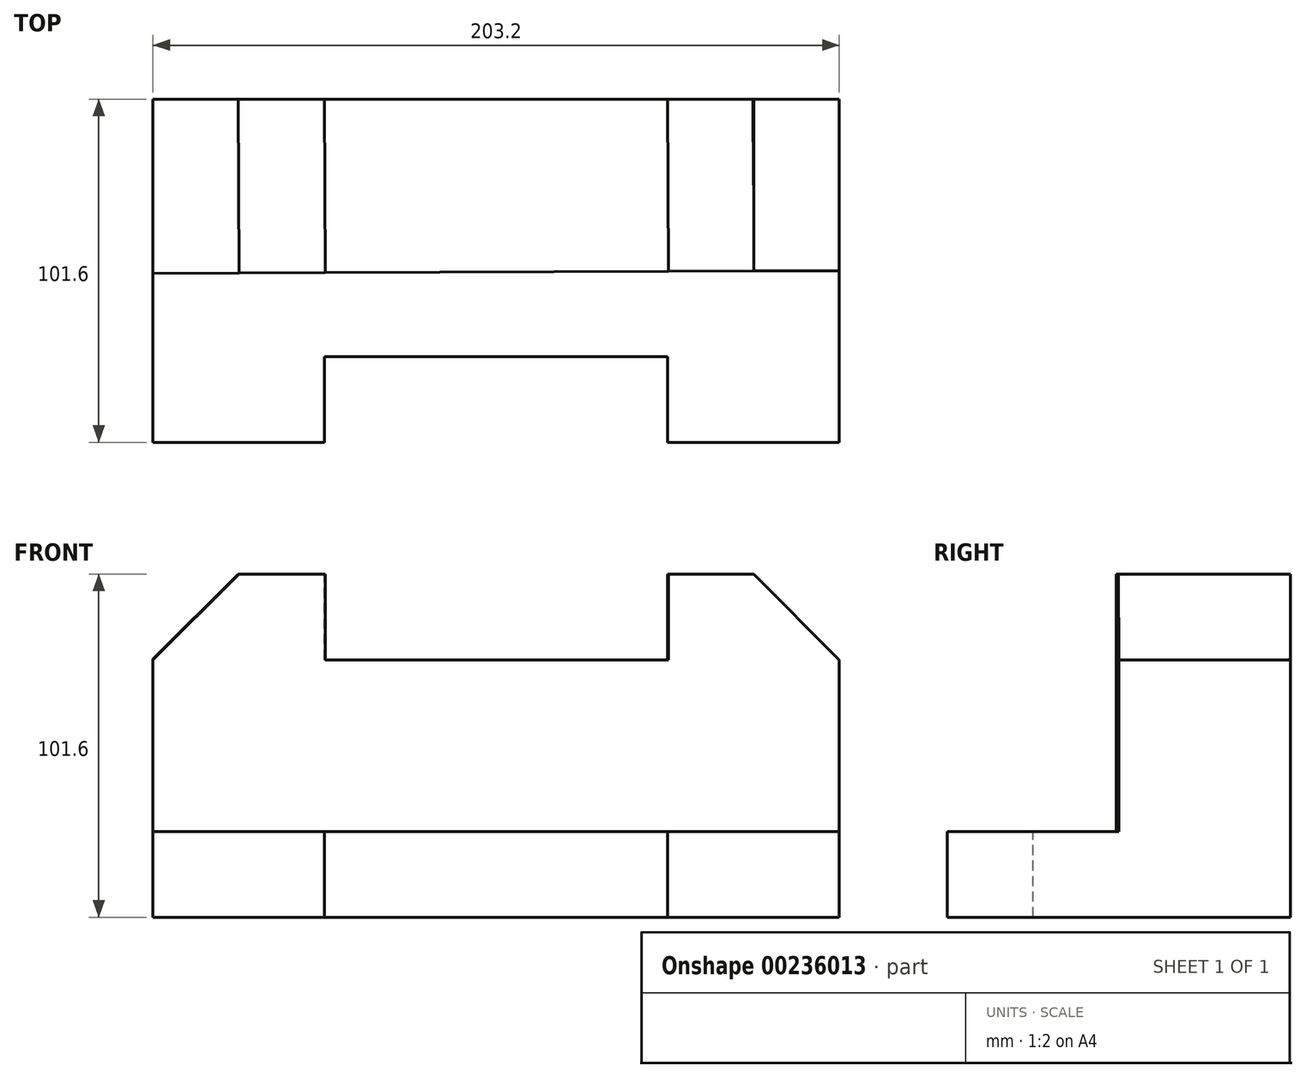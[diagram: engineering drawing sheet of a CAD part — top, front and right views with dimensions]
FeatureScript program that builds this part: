
annotation { "Feature Type Name" : "Feature", "Feature Type Description" : "" }
export const myFeature = defineFeature(function(context is Context, id is Id, definition is map)
    precondition{}
    {
        {
            var Q0;
            Q0=qCreatedBy(makeId("Top.planeOp"),FACE);
            var sketch = newSketch(context, id + "F0", { "sketchPlane" : qUnion([Q0])});
            skLineSegment(sketch, "E0.bottom", {"start": v(-129.83, -49.96) * mm, "end": v(73.37, -49.96) * mm});
            skLineSegment(sketch, "E0.top", {"start": v(-129.83, 51.64) * mm, "end": v(73.37, 51.64) * mm});
            skLineSegment(sketch, "E0.left", {"start": v(-129.83, -49.96) * mm, "end": v(-129.83, 51.64) * mm});
            skLineSegment(sketch, "E0.right", {"start": v(73.37, -49.96) * mm, "end": v(73.37, 51.64) * mm});
            skSolve(sketch);
        }
        {
            var Q0;
            Q0=makeQuery(id+"F0.imprint","IMPRINT",FACE,{"disambiguationData":[TD([[makeQuery(id+"F0.imprint","IMPRINT",EDGE,{"derivedFrom":sQuery(id+"F0.wireOp",EDGE,"E0.bottom")}),1.0]])]});
            extrude(context, id + "F1", {"entities" : qUnion([Q0]), "depth" : 101.6 * mm});
        }
        {
            var Q0;
            Q0=makeQuery(id+"F1.opExtrude","CAP_FACE",FACE,{"disambiguationData":[OSD([sQuery(id+"F0.wireOp",EDGE,"E0.bottom"),sQuery(id+"F0.wireOp",EDGE,"E0.top"),sQuery(id+"F0.wireOp",EDGE,"E0.left"),sQuery(id+"F0.wireOp",EDGE,"E0.right")])],"isStart":false});
            var sketch = newSketch(context, id + "F2", { "sketchPlane" : qUnion([Q0])});
            skLineSegment(sketch, "E1", {"start": v(73.37, -49.96) * mm, "end": v(73.37, 0.84) * mm});
            skLineSegment(sketch, "E2", {"start": v(73.37, 0.84) * mm, "end": v(-129.83, 0) * mm});
            skSolve(sketch);
        }
        {
            var Q0;
            Q0=makeQuery(id+"F2.imprint","IMPRINT",FACE,{"disambiguationData":[TD([[makeQuery(id+"F2.imprint","IMPRINT",EDGE,{"derivedFrom":sQuery(id+"F2.wireOp",EDGE,"E1")}),1.0]])]});
            extrude(context, id + "F3", {"entities" : qUnion([Q0]), "operationType" : NewBodyOperationType.REMOVE, "oppositeDirection" : true, "depth" : 76.2 * mm});
        }
        {
            var Q0;
            Q0=makeQuery(id+"F3.boolean.opBoolean","COPY",FACE,{"derivedFrom":makeQuery(id+"F3.opExtrude","CAP_FACE",FACE,{"disambiguationData":[OSD([sQuery(id+"F0.wireOp",EDGE,"E0.bottom"),sQuery(id+"F0.wireOp",EDGE,"E0.left"),sQuery(id+"F2.wireOp",EDGE,"E1"),sQuery(id+"F2.wireOp",EDGE,"E2")])],"isStart":false})});
            var sketch = newSketch(context, id + "F4", { "sketchPlane" : qUnion([Q0])});
            skLineSegment(sketch, "E3", {"start": v(-129.83, -49.96) * mm, "end": v(-79.03, -49.96) * mm});
            skLineSegment(sketch, "E4", {"start": v(73.37, -49.96) * mm, "end": v(22.57, -49.96) * mm});
            skLineSegment(sketch, "E5", {"start": v(-79.03, -49.96) * mm, "end": v(22.57, -49.96) * mm});
            skLineSegment(sketch, "E6", {"start": v(-79.03, -49.96) * mm, "end": v(-79.03, -24.56) * mm});
            skLineSegment(sketch, "E7", {"start": v(22.57, -49.96) * mm, "end": v(22.57, -24.56) * mm});
            skLineSegment(sketch, "E8", {"start": v(-79.03, -24.56) * mm, "end": v(22.57, -24.56) * mm});
            skSolve(sketch);
        }
        {
            var Q0;
            Q0=makeQuery(id+"F4.imprint","IMPRINT",FACE,{"disambiguationData":[TD([[makeQuery(id+"F4.imprint","IMPRINT",EDGE,{"derivedFrom":sQuery(id+"F4.wireOp",EDGE,"E5")}),1.0]])]});
            extrude(context, id + "F5", {"entities" : qUnion([Q0]), "operationType" : NewBodyOperationType.REMOVE, "oppositeDirection" : true, "depth" : 25.4 * mm});
        }
        {
            var Q0;
            Q0=makeQuery(id+"F1.opExtrude","CAP_FACE",FACE,{"disambiguationData":[OSD([sQuery(id+"F0.wireOp",EDGE,"E0.bottom"),sQuery(id+"F0.wireOp",EDGE,"E0.top"),sQuery(id+"F0.wireOp",EDGE,"E0.left"),sQuery(id+"F0.wireOp",EDGE,"E0.right")])],"isStart":false});
            var sketch = newSketch(context, id + "F6", { "sketchPlane" : qUnion([Q0])});
            skLineSegment(sketch, "E9", {"start": v(73.37, 51.64) * mm, "end": v(22.57, 51.64) * mm});
            skLineSegment(sketch, "E10", {"start": v(-129.83, 51.64) * mm, "end": v(-79.03, 51.64) * mm});
            skLineSegment(sketch, "E11", {"start": v(-79.03, 51.64) * mm, "end": v(-78.82, 0) * mm});
            skLineSegment(sketch, "E12", {"start": v(22.57, 51.64) * mm, "end": v(22.78, 0) * mm});
            skLineSegment(sketch, "E13", {"start": v(-79.03, 51.64) * mm, "end": v(22.57, 51.64) * mm});
            skSolve(sketch);
        }
        {
            var Q0;
            {var subQ0=sQuery(id+"F6.wireOp",EDGE,"E13");Q0=makeQuery(id+"F6.imprint","IMPRINT",FACE,{"disambiguationData":[TD([[makeQuery(id+"F6.imprint","IMPRINT",EDGE,{"derivedFrom":subQ0}),-1.0]])]});}
            extrude(context, id + "F7", {"entities" : qUnion([Q0]), "operationType" : NewBodyOperationType.REMOVE, "oppositeDirection" : true, "depth" : 25.4 * mm});
        }
        {
            var Q0;
            Q0=makeQuery(id+"F3.boolean.opBoolean","COPY",FACE,{"derivedFrom":makeQuery(id+"F3.opExtrude","SWEPT_FACE",FACE,{"disambiguationData":[OSD([sQuery(id+"F2.wireOp",EDGE,"E2")])]})});
            var sketch = newSketch(context, id + "F8", { "sketchPlane" : qUnion([Q0])});
            skLineSegment(sketch, "E14", {"start": v(22.78, 76.2) * mm, "end": v(73.37, 76.2) * mm});
            skLineSegment(sketch, "E15", {"start": v(48.08, 101.6) * mm, "end": v(73.37, 76.2) * mm});
            skSolve(sketch);
        }
        {
            var Q0;
            {var subQ0=sQuery(id+"F8.wireOp",EDGE,"E15");Q0=makeQuery(id+"F8.imprint","IMPRINT",FACE,{"disambiguationData":[TD([[makeQuery(id+"F8.imprint","IMPRINT",EDGE,{"derivedFrom":subQ0}),1.0]])]});}
            extrude(context, id + "F9", {"entities" : qUnion([Q0]), "operationType" : NewBodyOperationType.REMOVE, "oppositeDirection" : true, "depth" : 50.8 * mm});
        }
        {
            var Q0;
            Q0=makeQuery(id+"F1.opExtrude","SWEPT_FACE",FACE,{"disambiguationData":[OSD([sQuery(id+"F0.wireOp",EDGE,"E0.right")])]});
            var sketch = newSketch(context, id + "F10", { "sketchPlane" : qUnion([Q0])});
            skLineSegment(sketch, "E16", {"start": v(0.84, 76.2) * mm, "end": v(51.64, 76.2) * mm});
            skSolve(sketch);
        }
        {
            var Q0;
            {var subQ0=sQuery(id+"F10.wireOp",EDGE,"E16");Q0=makeQuery(id+"F10.imprint","IMPRINT",FACE,{"disambiguationData":[TD([[makeQuery(id+"F10.imprint","IMPRINT",EDGE,{"derivedFrom":subQ0}),1.0]])]});}
            extrude(context, id + "F11", {"entities" : qUnion([Q0]), "operationType" : NewBodyOperationType.REMOVE, "oppositeDirection" : true, "depth" : 25.4 * mm});
        }
        {
            var Q0;
            Q0=makeQuery(id+"F11.boolean.opBoolean","COPY",FACE,{"derivedFrom":makeQuery(id+"F11.opExtrude","SWEPT_FACE",FACE,{"disambiguationData":[OSD([sQuery(id+"F0.wireOp",EDGE,"E0.right"),sQuery(id+"F2.wireOp",EDGE,"E1"),sQuery(id+"F2.wireOp",EDGE,"E2")])]})});
            extrude(context, id + "F12", {"entities" : qUnion([Q0]), "operationType" : NewBodyOperationType.ADD, "depth" : 50.8 * mm});
        }
        {
            var Q0;
            Q0=makeQuery(id+"F3.boolean.opBoolean","COPY",FACE,{"derivedFrom":makeQuery(id+"F3.opExtrude","SWEPT_FACE",FACE,{"disambiguationData":[OSD([sQuery(id+"F2.wireOp",EDGE,"E2")])]})});
            var sketch = newSketch(context, id + "F13", { "sketchPlane" : qUnion([Q0])});
            skLineSegment(sketch, "E17", {"start": v(-78.82, 76.2) * mm, "end": v(-129.83, 76.2) * mm});
            skLineSegment(sketch, "E18", {"start": v(-78.82, 101.6) * mm, "end": v(-104.32, 101.6) * mm});
            skLineSegment(sketch, "E19", {"start": v(-104.32, 101.6) * mm, "end": v(-129.83, 76.2) * mm});
            skSolve(sketch);
        }
        {
            var Q0;
            {var subQ0=sQuery(id+"F13.wireOp",EDGE,"E19");Q0=makeQuery(id+"F13.imprint","IMPRINT",FACE,{"disambiguationData":[TD([[makeQuery(id+"F13.imprint","IMPRINT",EDGE,{"derivedFrom":subQ0}),-1.0]])]});}
            extrude(context, id + "F14", {"entities" : qUnion([Q0]), "operationType" : NewBodyOperationType.REMOVE, "oppositeDirection" : true, "depth" : 50.8 * mm});
        }
        {
            var Q0;
            Q0=makeQuery(id+"F14.boolean.opBoolean","COPY",FACE,{"derivedFrom":makeQuery(id+"F14.opExtrude","CAP_FACE",FACE,{"disambiguationData":[OSD([sQuery(id+"F0.wireOp",EDGE,"E0.left"),sQuery(id+"F2.wireOp",EDGE,"E2"),sQuery(id+"F13.wireOp",EDGE,"E19")])],"isStart":false})});
            extrude(context, id + "F15", {"entities" : qUnion([Q0]), "operationType" : NewBodyOperationType.REMOVE, "oppositeDirection" : true, "depth" : 25.4 * mm});
        }
    });
